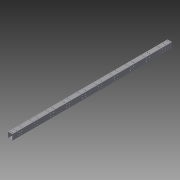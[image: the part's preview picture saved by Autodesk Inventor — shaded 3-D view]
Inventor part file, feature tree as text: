
AUTODESK INVENTOR PART (.ipt)
format: ipt  version: 2015 SP1 (Build 190203100, 203)  size: 296,960 bytes
history: native  units: in
note: dims shown in document units (in); Inventor stores cm internally (conversion verified against a paired STEP export)
features: extrude x4, sketch x3
ambient origin geometry x8: Origin, YZ Plane, XZ Plane, XY Plane, X Axis, Y Axis, Z Axis, Center Point
bodies: Solid1 (feature_tree)
feature tree (7):
  extrude  "Extrusion1"  Depth=1.9685in
  extrude  "Extrusion2"  Depth=56.2992in TaperAngle=0.0deg
  extrude  "Extrusion3"  Depth=0.0787in
  extrude  "Extrusion4"  Depth=0.0787in
  sketch  "Sketch3"  dims[d0=1.5748in d1=1.9685in]
  sketch  "Sketch4"  dims[d3=0.0787in d4=56.2992in d5=0.0in]
  sketch  "Sketch5"  dims[d6=0.0787in d7=0.0787in d8=0.0787in d9=0.2756in d10=0.9843in d11=0.7874in d12=0.5118in d13=2.3228in d14=3.937in d16=5.6299in d17=0.3937in d19=0.3937in d21=0.3937in d22=0.0in d23=0.2756in d24=0.4921in d25=0.7087in d26=0.4921in d27=0.0in d28=0.0in d29=0.3937in d30=0.7087in d31=1.8307in d32=0.2756in d33=1.9685in d34=3.937in d36=5.6299in d37=0.3937in d39=0.3937in d41=0.0in d42=0.0in]
